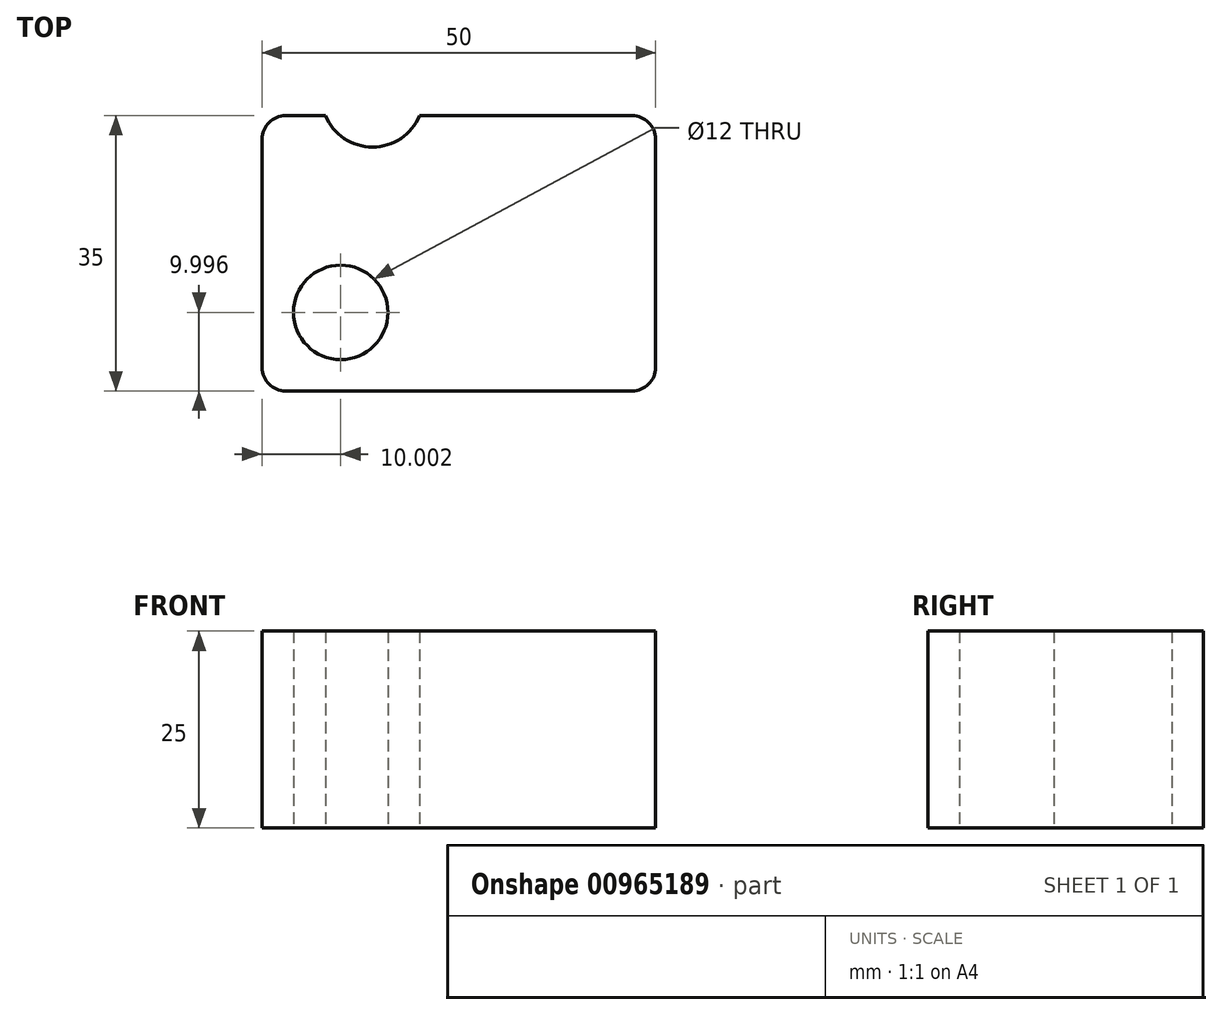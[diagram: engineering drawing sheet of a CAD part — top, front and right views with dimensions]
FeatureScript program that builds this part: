
annotation { "Feature Type Name" : "Feature", "Feature Type Description" : "" }
export const myFeature = defineFeature(function(context is Context, id is Id, definition is map)
    precondition{}
    {
        {
            var Q0;
            Q0=qCreatedBy(makeId("Top.planeOp"),FACE);
            var sketch = newSketch(context, id + "F0", { "sketchPlane" : qUnion([Q0])});
            skLineSegment(sketch, "E0.bottom", {"start": v(-30.97, 9.5) * mm, "end": v(19.03, 9.5) * mm});
            skLineSegment(sketch, "E0.top", {"start": v(-30.97, -25.5) * mm, "end": v(19.03, -25.5) * mm});
            skLineSegment(sketch, "E0.left", {"start": v(-30.97, 9.5) * mm, "end": v(-30.97, -25.5) * mm});
            skLineSegment(sketch, "E0.right", {"start": v(19.03, 9.5) * mm, "end": v(19.03, -25.5) * mm});
            skCircle(sketch, "E1", {"center": v(-20.97, -15.5) * mm, "radius": 6 * mm});
            skCircle(sketch, "E2", {"center": v(-16.93, 11.96) * mm, "radius": 6.46 * mm});
            skSolve(sketch);
        }
        {
            var Q0;
            Q0=makeQuery(id+"F0.imprint","IMPRINT",FACE,{"disambiguationData":[TD([[makeQuery(id+"F0.imprint","IMPRINT",EDGE,{"derivedFrom":sQuery(id+"F0.wireOp",EDGE,"E0.top")}),1.0]])]});
            var Q1;
            {var subQ0=sQuery(id+"F0.wireOp",EDGE,"E2");var subQ1=sQuery(id+"F0.wireOp",EDGE,"E0.bottom");var subQ2=makeQuery(id+"F0.imprint","INTERSECT",VERTEX,{"disambiguationData":[OD(0.0)],"derivedFrom":[subQ1,subQ0]});Q1=makeQuery(id+"F0.imprint","IMPRINT",FACE,{"disambiguationData":[TD([[makeQuery(id+"F0.imprint","IMPRINT",EDGE,{"disambiguationData":[TD([[subQ2,-1.0]])],"derivedFrom":subQ1}),-1.0]])]});}
            var Q2;
            {var subQ0=sQuery(id+"F0.wireOp",EDGE,"E2");var subQ1=sQuery(id+"F0.wireOp",EDGE,"E0.bottom");var subQ2=makeQuery(id+"F0.imprint","INTERSECT",VERTEX,{"disambiguationData":[OD(0.0)],"derivedFrom":[subQ1,subQ0]});Q2=makeQuery(id+"F0.imprint","IMPRINT",FACE,{"disambiguationData":[TD([[makeQuery(id+"F0.imprint","IMPRINT",EDGE,{"disambiguationData":[TD([[subQ2,-1.0]])],"derivedFrom":subQ1}),1.0]])]});}
            extrude(context, id + "F1", {"entities" : qUnion([Q0, Q1, Q2]), "depth" : 25 * mm, "offsetDistance" : 25 * mm});
        }
        {
            var Q0;
            Q0=makeQuery(id+"F1.opExtrude","SWEPT_EDGE",EDGE,{"disambiguationData":[OSD([sQuery(id+"F0.wireOp",EDGE,"E0.bottom"),sQuery(id+"F0.wireOp",EDGE,"E0.left")])]});
            var Q1;
            Q1=makeQuery(id+"F1.opExtrude","SWEPT_EDGE",EDGE,{"disambiguationData":[OSD([sQuery(id+"F0.wireOp",EDGE,"E0.top"),sQuery(id+"F0.wireOp",EDGE,"E0.left")])]});
            var Q2;
            Q2=makeQuery(id+"F1.opExtrude","SWEPT_EDGE",EDGE,{"disambiguationData":[OSD([sQuery(id+"F0.wireOp",EDGE,"E0.top"),sQuery(id+"F0.wireOp",EDGE,"E0.right")])]});
            var Q3;
            Q3=makeQuery(id+"F1.opExtrude","SWEPT_EDGE",EDGE,{"disambiguationData":[OSD([sQuery(id+"F0.wireOp",EDGE,"E0.bottom"),sQuery(id+"F0.wireOp",EDGE,"E0.right")])]});
            fillet(context, id + "F2", {"entities" : qUnion([Q0, Q1, Q2, Q3]), "radius" : 3 * mm, "tangentPropagation" : true, "allowEdgeOverflow" : false});
        }
    });
